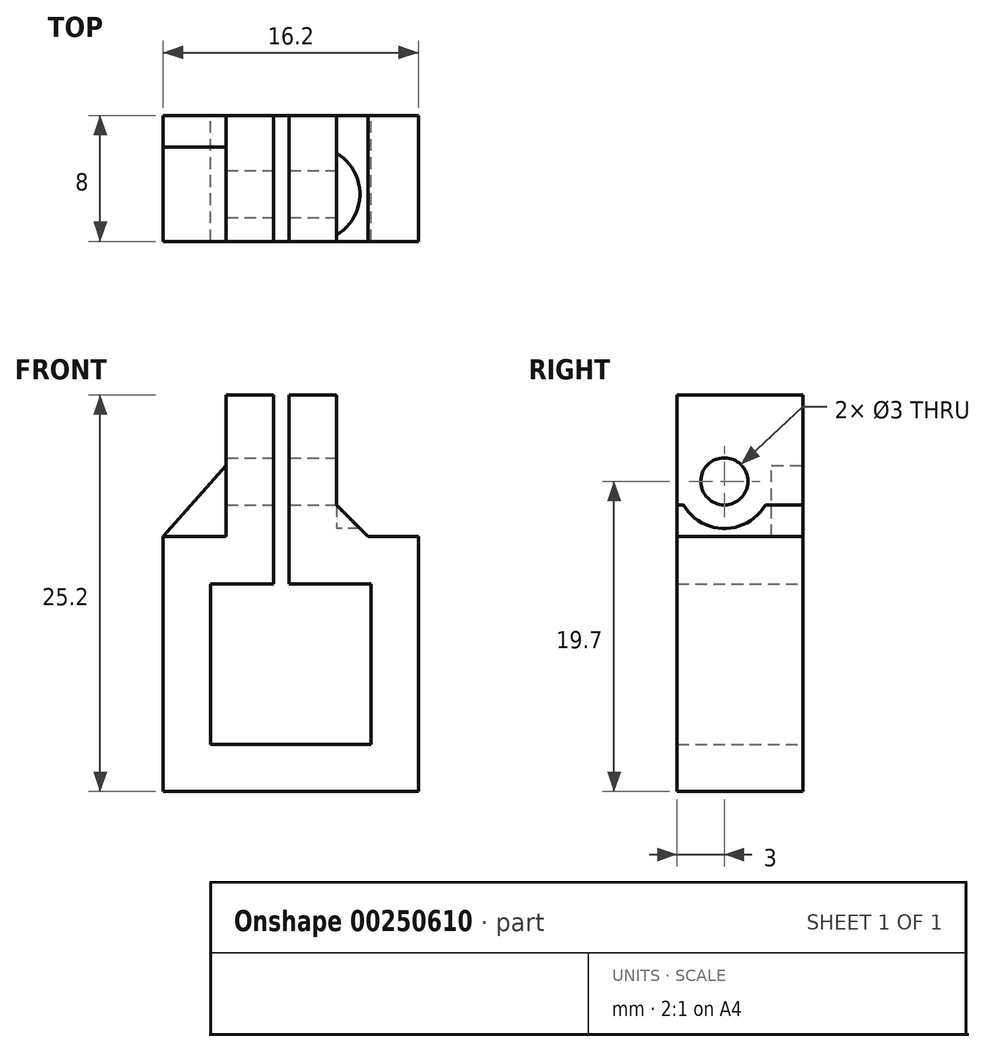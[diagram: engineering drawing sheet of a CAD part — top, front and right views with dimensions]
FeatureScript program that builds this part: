
annotation { "Feature Type Name" : "Feature", "Feature Type Description" : "" }
export const myFeature = defineFeature(function(context is Context, id is Id, definition is map)
    precondition{}
    {
        {
            var Q0;
            Q0=qCreatedBy(makeId("Front.planeOp"),FACE);
            var sketch = newSketch(context, id + "F0", { "sketchPlane" : qUnion([Q0])});
            skLineSegment(sketch, "E0.rect.bottom", {"start": v(5.1, -5.1) * mm, "end": v(-5.1, -5.1) * mm});
            skLineSegment(sketch, "E0.rect.top", {"start": v(5.1, 5.1) * mm, "end": v(-0.1, 5.1) * mm});
            skLineSegment(sketch, "E0.rect.left", {"start": v(5.1, -5.1) * mm, "end": v(5.1, 5.1) * mm});
            skLineSegment(sketch, "E0.rect.right", {"start": v(-5.1, -5.1) * mm, "end": v(-5.1, 5.1) * mm});
            skPoint(sketch, "E0.rect.middle", {"position": v(0, 0) * mm});
            skLineSegment(sketch, "E1.0", {"start": v(8.1, 8.1) * mm, "end": v(2.9, 8.1) * mm});
            skLineSegment(sketch, "E1.1", {"start": v(8.1, -8.1) * mm, "end": v(8.1, 8.1) * mm});
            skLineSegment(sketch, "E1.2", {"start": v(8.1, -8.1) * mm, "end": v(-8.1, -8.1) * mm});
            skLineSegment(sketch, "E1.3", {"start": v(-8.1, -8.1) * mm, "end": v(-8.1, 8.1) * mm});
            skLineSegment(sketch, "E2", {"start": v(-4.1, 8.1) * mm, "end": v(-4.1, 17.1) * mm});
            skLineSegment(sketch, "E3", {"start": v(-4.1, 17.1) * mm, "end": v(-1.1, 17.1) * mm});
            skLineSegment(sketch, "E4", {"start": v(-1.1, 17.1) * mm, "end": v(-1.1, 8.1) * mm});
            skLineSegment(sketch, "E5", {"start": v(-0.1, 17.1) * mm, "end": v(-0.1, 8.1) * mm});
            skLineSegment(sketch, "E6", {"start": v(-0.1, 17.1) * mm, "end": v(2.9, 17.1) * mm});
            skLineSegment(sketch, "E7", {"start": v(2.9, 17.1) * mm, "end": v(2.9, 8.1) * mm});
            skLineSegment(sketch, "E8", {"start": v(-4.1, 8.1) * mm, "end": v(-5.1, 8.1) * mm});
            skLineSegment(sketch, "E9", {"start": v(-8.1, 8.1) * mm, "end": v(-4.1, 8.1) * mm});
            skPoint(sketch, "E10.end.orphan", {"position": v(-5.1, 17.1) * mm});
            skLineSegment(sketch, "E11", {"start": v(-4.1, 5.1) * mm, "end": v(-5.1, 5.1) * mm});
            skLineSegment(sketch, "E12", {"start": v(-1.1, 8.1) * mm, "end": v(-1.1, 5.1) * mm});
            skLineSegment(sketch, "E13", {"start": v(-0.1, 8.1) * mm, "end": v(-0.1, 5.1) * mm});
            skPoint(sketch, "E13.endSnap0", {"position": v(0.5, 5.1) * mm});
            skLineSegment(sketch, "E14.trimOffspring", {"start": v(-1.1, 5.1) * mm, "end": v(-4.1, 5.1) * mm});
            skSolve(sketch);
        }
        {
            var Q0;
            Q0=qSketchRegion(id+"F0",true);
            extrude(context, id + "F1", {"entities" : qUnion([Q0]), "depth" : 8 * mm});
        }
        {
            var Q0;
            Q0=makeQuery(id+"F1.opExtrude","SWEPT_FACE",FACE,{"disambiguationData":[OSD([sQuery(id+"F0.wireOp",EDGE,"E4")])]});
            var sketch = newSketch(context, id + "F2", { "sketchPlane" : qUnion([Q0])});
            skCircle(sketch, "E15", {"center": v(-5, 11.6) * mm, "radius": 1.5 * mm});
            skPoint(sketch, "E15.centerSnap0", {"position": v(-9, 11.6) * mm});
            skPoint(sketch, "E15.centerSnap1", {"position": v(-5, 16.1) * mm});
            skSolve(sketch);
        }
        {
            var Q0;
            Q0=qSketchRegion(id+"F2",true);
            extrude(context, id + "F3", {"entities" : qUnion([Q0]), "operationType" : NewBodyOperationType.REMOVE, "endBound" : BoundingType.SYMMETRIC, "oppositeDirection" : true, "depth" : 25 * mm});
        }
        {
            var Q0;
            Q0=makeQuery(id+"F1.opExtrude","SWEPT_EDGE",EDGE,{"disambiguationData":[OSD([sQuery(id+"F0.wireOp",EDGE,"E1.0"),sQuery(id+"F0.wireOp",EDGE,"E7")])]});
            chamfer(context, id + "F4", {"entities" : qUnion([Q0]), "width" : 2 * mm, "tangentPropagation" : true});
        }
        {
            var Q0;
            Q0=makeQuery(id+"F1.opExtrude","SWEPT_FACE",FACE,{"disambiguationData":[OSD([sQuery(id+"F0.wireOp",EDGE,"E7")])]});
            var sketch = newSketch(context, id + "F5", { "sketchPlane" : qUnion([Q0])});
            skCircle(sketch, "E16", {"center": v(-5, 11.6) * mm, "radius": 3 * mm});
            skSolve(sketch);
        }
        {
            var Q0;
            Q0=qSketchRegion(id+"F5",true);
            extrude(context, id + "F6", {"entities" : qUnion([Q0]), "operationType" : NewBodyOperationType.REMOVE, "depth" : 4 * mm});
        }
        {
            var Q0;
            Q0=makeQuery(id+"F1.opExtrude","CAP_FACE",FACE,{"disambiguationData":[OSD([sQuery(id+"F0.wireOp",EDGE,"E0.rect.bottom"),sQuery(id+"F0.wireOp",EDGE,"E0.rect.top"),sQuery(id+"F0.wireOp",EDGE,"E0.rect.left"),sQuery(id+"F0.wireOp",EDGE,"E0.rect.right"),sQuery(id+"F0.wireOp",EDGE,"E1.0"),sQuery(id+"F0.wireOp",EDGE,"E1.1"),sQuery(id+"F0.wireOp",EDGE,"E1.2"),sQuery(id+"F0.wireOp",EDGE,"E1.3"),sQuery(id+"F0.wireOp",EDGE,"E2"),sQuery(id+"F0.wireOp",EDGE,"E3"),sQuery(id+"F0.wireOp",EDGE,"E4"),sQuery(id+"F0.wireOp",EDGE,"E5"),sQuery(id+"F0.wireOp",EDGE,"E6"),sQuery(id+"F0.wireOp",EDGE,"E7"),sQuery(id+"F0.wireOp",EDGE,"E9"),sQuery(id+"F0.wireOp",EDGE,"E11"),sQuery(id+"F0.wireOp",EDGE,"E12"),sQuery(id+"F0.wireOp",EDGE,"E13"),sQuery(id+"F0.wireOp",EDGE,"E14.trimOffspring")])],"isStart":true});
            var sketch = newSketch(context, id + "F7", { "sketchPlane" : qUnion([Q0])});
            skLineSegment(sketch, "E17", {"start": v(8.1, 8.1) * mm, "end": v(4.1, 12.6) * mm});
            skLineSegment(sketch, "E18", {"start": v(4.1, 12.6) * mm, "end": v(4.1, 8.1) * mm});
            skLineSegment(sketch, "E19", {"start": v(4.1, 8.1) * mm, "end": v(8.1, 8.1) * mm});
            skSolve(sketch);
        }
        {
            var Q0;
            Q0=qSketchRegion(id+"F7",true);
            extrude(context, id + "F8", {"entities" : qUnion([Q0]), "oppositeDirection" : true, "depth" : 2 * mm});
        }
    });
